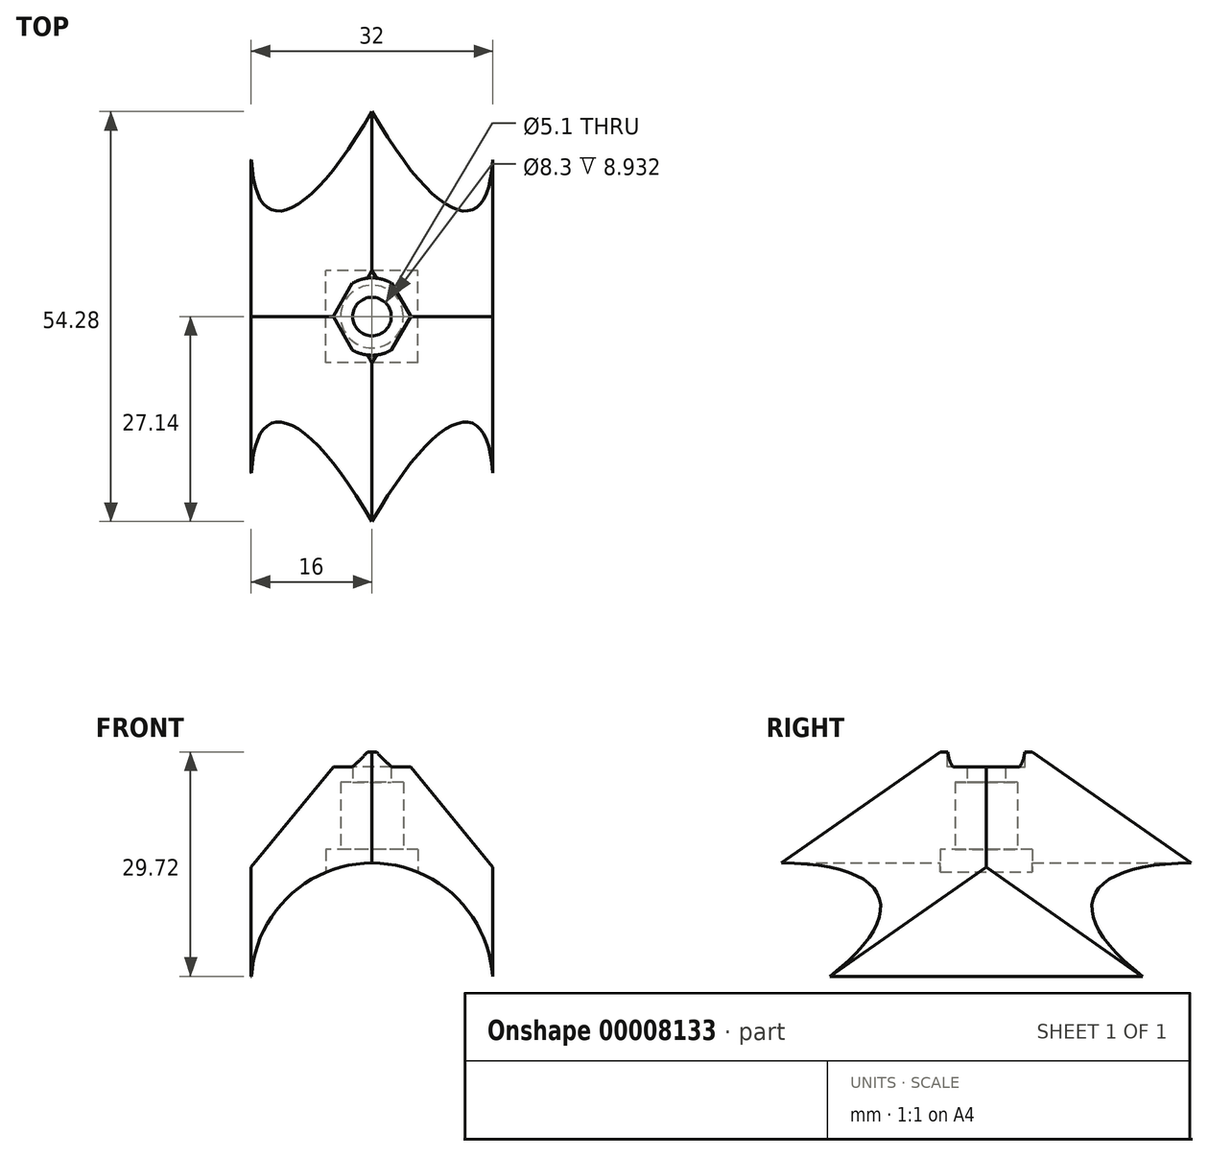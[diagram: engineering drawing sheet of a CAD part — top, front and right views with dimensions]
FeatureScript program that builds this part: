
annotation { "Feature Type Name" : "Feature", "Feature Type Description" : "" }
export const myFeature = defineFeature(function(context is Context, id is Id, definition is map)
    precondition{}
    {
        {
            var Q0;
            Q0=qCreatedBy(makeId("Front.planeOp"),FACE);
            var sketch = newSketch(context, id + "F0", { "sketchPlane" : qUnion([Q0])});
            skCircle(sketch, "E0", {"center": v(0, 0) * mm, "radius": 16 * mm});
            skSolve(sketch);
        }
        {
            var Q0;
            Q0=qSketchRegion(id+"F0",true);
            extrude(context, id + "F1", {"entities" : qUnion([Q0]), "endBound" : BoundingType.SYMMETRIC, "depth" : 200 * mm});
        }
        {
            var Q0;
            Q0=qCreatedBy(makeId("Top.planeOp"),FACE);
            var sketch = newSketch(context, id + "F2", { "sketchPlane" : qUnion([Q0])});
            skLineSegment(sketch, "E1.rect.bottom", {"start": v(6.1, 6.1) * mm, "end": v(-6.1, 6.1) * mm});
            skLineSegment(sketch, "E1.rect.top", {"start": v(6.1, -6.1) * mm, "end": v(-6.1, -6.1) * mm});
            skLineSegment(sketch, "E1.rect.left", {"start": v(6.1, 6.1) * mm, "end": v(6.1, -6.1) * mm});
            skLineSegment(sketch, "E1.rect.right", {"start": v(-6.1, 6.1) * mm, "end": v(-6.1, -6.1) * mm});
            skPoint(sketch, "E1.rect.middle", {"position": v(0, 0) * mm});
            skSolve(sketch);
        }
        {
            var Q0;
            Q0=qSketchRegion(id+"F2",true);
            extrude(context, id + "F3", {"entities" : qUnion([Q0]), "operationType" : NewBodyOperationType.ADD, "depth" : 17.8 * mm});
        }
        {
            var Q0;
            Q0=makeQuery(id+"F3.opExtrude","CAP_FACE",FACE,{"disambiguationData":[OSD([sQuery(id+"F2.wireOp",EDGE,"E1.rect.bottom"),sQuery(id+"F2.wireOp",EDGE,"E1.rect.top"),sQuery(id+"F2.wireOp",EDGE,"E1.rect.left"),sQuery(id+"F2.wireOp",EDGE,"E1.rect.right")])],"isStart":false});
            var sketch = newSketch(context, id + "F4", { "sketchPlane" : qUnion([Q0])});
            skCircle(sketch, "E2", {"center": v(0, 0) * mm, "radius": 4.15 * mm});
            skSolve(sketch);
        }
        {
            var Q0;
            Q0=qSketchRegion(id+"F4",true);
            extrude(context, id + "F5", {"entities" : qUnion([Q0]), "operationType" : NewBodyOperationType.ADD, "depth" : 8.93 * mm});
        }
        {
            var Q0;
            Q0=qCreatedBy(makeId("Right.planeOp"),FACE);
            var sketch = newSketch(context, id + "F6", { "sketchPlane" : qUnion([Q0])});
            skLineSegment(sketch, "E3", {"start": v(0, 0) * mm, "end": v(0, 35) * mm});
            skLineSegment(sketch, "E4", {"start": v(0, 0) * mm, "end": v(-50, 0) * mm});
            skLineSegment(sketch, "E5", {"start": v(0, 0) * mm, "end": v(50, 0) * mm});
            skLineSegment(sketch, "E6", {"start": v(0, 35) * mm, "end": v(-50, 0) * mm});
            skLineSegment(sketch, "E7", {"start": v(0, 35) * mm, "end": v(50, 0) * mm});
            skSolve(sketch);
        }
        {
            var Q0;
            Q0 = qSketchRegion(id + "F6", true);
            extrude(context, id + "F7", {"entities" : qUnion([Q0]), "endBound" : BoundingType.SYMMETRIC, "depth" : 32 * mm});
        }
        {
            var Q0;
            Q0=makeQuery(id+"F7.opExtrude","CAP_EDGE",EDGE,{"disambiguationData":[OSD([sQuery(id+"F6.wireOp",EDGE,"E7")])],"isStart":true});
            var Q1;
            Q1=makeQuery(id+"F7.opExtrude","CAP_EDGE",EDGE,{"disambiguationData":[OSD([sQuery(id+"F6.wireOp",EDGE,"E6")])],"isStart":true});
            var Q2;
            Q2=makeQuery(id+"F7.opExtrude","CAP_EDGE",EDGE,{"disambiguationData":[OSD([sQuery(id+"F6.wireOp",EDGE,"E6")])],"isStart":false});
            var Q3;
            Q3=makeQuery(id+"F7.opExtrude","CAP_EDGE",EDGE,{"disambiguationData":[OSD([sQuery(id+"F6.wireOp",EDGE,"E7")])],"isStart":false});
            chamfer(context, id + "F8", {"entities" : qUnion([Q0, Q1, Q2, Q3]), "width" : 16 * mm, "tangentPropagation" : true});
        }
        {
            var Q0;
            Q0=makeQuery(id+"F1.opExtrude","SWEPT_BODY",BODY,{"disambiguationData":[OSD([sQuery(id+"F0.wireOp",EDGE,"E0")])]});
            var Q1;
            Q1=makeQuery(id+"F7.opExtrude","SWEPT_BODY",BODY,{"disambiguationData":[OSD([sQuery(id+"F6.wireOp",EDGE,"E4"),sQuery(id+"F6.wireOp",EDGE,"E5"),sQuery(id+"F6.wireOp",EDGE,"E6"),sQuery(id+"F6.wireOp",EDGE,"E7")])]});
            booleanBodies(context, id + "F9", {"operationType" : BooleanOperationType.SUBTRACTION, "tools" : qUnion([Q0]), "targets" : qUnion([Q1])});
        }
        {
            var Q0;
            Q0=makeQuery(id+"F9.opBoolean","COPY",FACE,{"derivedFrom":makeQuery(id+"F5.opExtrude","CAP_FACE",FACE,{"disambiguationData":[OSD([sQuery(id+"F4.wireOp",EDGE,"E2")])],"isStart":false})});
            var sketch = newSketch(context, id + "F10", { "sketchPlane" : qUnion([Q0])});
            skCircle(sketch, "E8", {"center": v(0, 0) * mm, "radius": 2.55 * mm});
            skSolve(sketch);
        }
        {
            var Q0;
            Q0 = qSketchRegion(id + "F10", true);
            extrude(context, id + "F11", {"entities" : qUnion([Q0]), "operationType" : NewBodyOperationType.REMOVE, "oppositeDirection" : true, "depth" : 25 * mm});
        }
        {
            var Q0;
            Q0=makeQuery(id+"F9.opBoolean","COPY",FACE,{"derivedFrom":makeQuery(id+"F3.opExtrude","CAP_FACE",FACE,{"disambiguationData":[OSD([sQuery(id+"F2.wireOp",EDGE,"E1.rect.bottom"),sQuery(id+"F2.wireOp",EDGE,"E1.rect.top"),sQuery(id+"F2.wireOp",EDGE,"E1.rect.left"),sQuery(id+"F2.wireOp",EDGE,"E1.rect.right")])],"isStart":false})});
            cPlane(context, id + "F12", {"entities" : qUnion([Q0]), "cplaneType" : CPlaneType.OFFSET, "offset" : 12.93 * mm, "oppositeDirection" : true, "width" : 150 * mm, "height" : 150 * mm});
        }
        {
            var Q0;
            Q0=qCreatedBy(id+"F12.planeOp",FACE);
            var sketch = newSketch(context, id + "F13", { "sketchPlane" : qUnion([Q0])});
            skLineSegment(sketch, "E9.rect.bottom", {"start": v(-23.77, 20) * mm, "end": v(23.77, 20) * mm});
            skLineSegment(sketch, "E9.rect.top", {"start": v(-23.77, -20) * mm, "end": v(23.77, -20) * mm});
            skLineSegment(sketch, "E9.rect.left", {"start": v(-23.77, 20) * mm, "end": v(-23.77, -20) * mm});
            skLineSegment(sketch, "E9.rect.right", {"start": v(23.77, 20) * mm, "end": v(23.77, -20) * mm});
            skPoint(sketch, "E9.rect.middle", {"position": v(0, 0) * mm});
            skSolve(sketch);
        }
        {
            var Q0;
            Q0 = qSketchRegion(id + "F13", true);
            extrude(context, id + "F14", {"entities" : qUnion([Q0]), "operationType" : NewBodyOperationType.REMOVE, "oppositeDirection" : true, "depth" : 25 * mm});
        }
        {
            var Q0;
            Q0=makeQuery(id+"F14.boolean.opBoolean","COPY",FACE,{"derivedFrom":makeQuery(id+"F14.opExtrude","CAP_FACE",FACE,{"disambiguationData":[OSD([sQuery(id+"F13.wireOp",EDGE,"E9.rect.bottom"),sQuery(id+"F13.wireOp",EDGE,"E9.rect.top"),sQuery(id+"F13.wireOp",EDGE,"E9.rect.left"),sQuery(id+"F13.wireOp",EDGE,"E9.rect.right")])],"isStart":true})});
            var sketch = newSketch(context, id + "F15", { "sketchPlane" : qUnion([Q0])});
            skCircle(sketch, "E10", {"center": v(0, 0) * mm, "radius": 5.12 * mm});
            skSolve(sketch);
        }
        {
            var Q0;
            Q0 = qSketchRegion(id + "F15", true);
            extrude(context, id + "F16", {"entities" : qUnion([Q0]), "operationType" : NewBodyOperationType.REMOVE, "oppositeDirection" : true, "depth" : 2 * mm});
        }
        {
            var Q0;
            Q0=qCreatedBy(makeId("Front.planeOp"),FACE);
            var sketch = newSketch(context, id + "F17", { "sketchPlane" : qUnion([Q0])});
            skLineSegment(sketch, "E11.rect.bottom", {"start": v(-16.62, 1) * mm, "end": v(16.62, 1) * mm});
            skLineSegment(sketch, "E11.rect.top", {"start": v(-16.62, -1) * mm, "end": v(16.62, -1) * mm});
            skLineSegment(sketch, "E11.rect.left", {"start": v(-16.62, 1) * mm, "end": v(-16.62, -1) * mm});
            skLineSegment(sketch, "E11.rect.right", {"start": v(16.62, 1) * mm, "end": v(16.62, -1) * mm});
            skPoint(sketch, "E11.rect.middle", {"position": v(0, 0) * mm});
            skSolve(sketch);
        }
        {
            var Q0;
            Q0 = qSketchRegion(id + "F17", true);
            extrude(context, id + "F18", {"entities" : qUnion([Q0]), "operationType" : NewBodyOperationType.REMOVE, "endBound" : BoundingType.SYMMETRIC, "oppositeDirection" : true, "depth" : 100 * mm});
        }
    });
